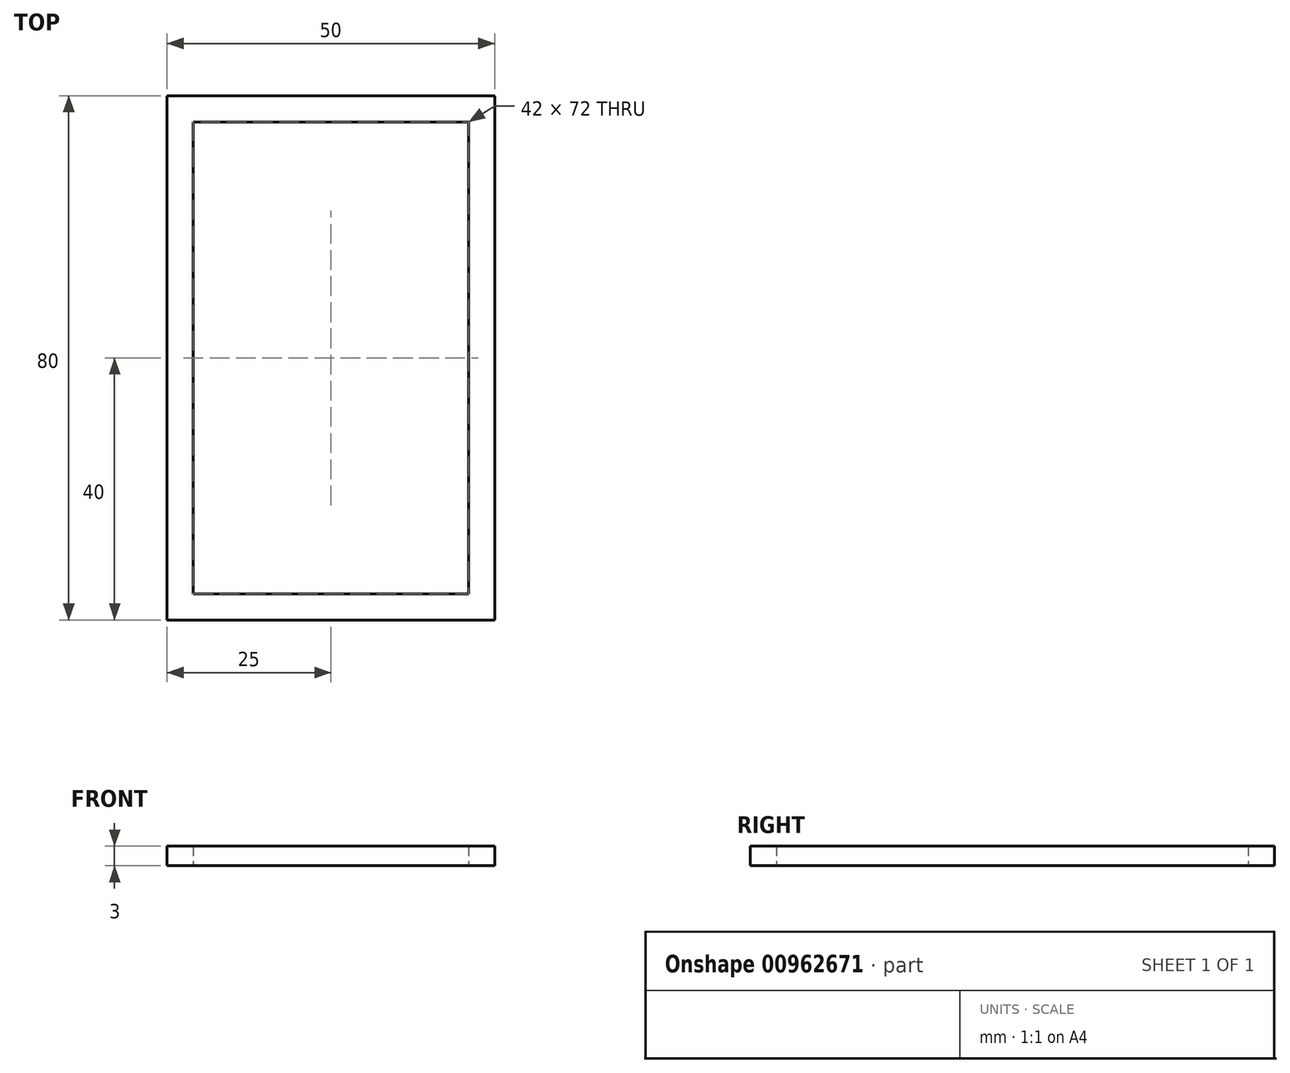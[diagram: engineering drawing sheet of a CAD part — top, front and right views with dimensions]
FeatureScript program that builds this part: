
annotation { "Feature Type Name" : "Feature", "Feature Type Description" : "" }
export const myFeature = defineFeature(function(context is Context, id is Id, definition is map)
    precondition{}
    {
        {
            var Q0;
            Q0=qCreatedBy(makeId("Top.planeOp"),FACE);
            var sketch = newSketch(context, id + "F0", { "sketchPlane" : qUnion([Q0])});
            skLineSegment(sketch, "E0", {"start": v(-25, 40) * mm, "end": v(-25, -40) * mm});
            skLineSegment(sketch, "E1", {"start": v(-25, -40) * mm, "end": v(25, -40) * mm});
            skLineSegment(sketch, "E2", {"start": v(25, -40) * mm, "end": v(25, 40) * mm});
            skLineSegment(sketch, "E3", {"start": v(25, 40) * mm, "end": v(-25, 40) * mm});
            skLineSegment(sketch, "E4", {"start": v(-21, 36) * mm, "end": v(-21, -36) * mm});
            skLineSegment(sketch, "E5", {"start": v(-21, -36) * mm, "end": v(21, -36) * mm});
            skLineSegment(sketch, "E6", {"start": v(21, -36) * mm, "end": v(21, 36) * mm});
            skLineSegment(sketch, "E7", {"start": v(21, 36) * mm, "end": v(-21, 36) * mm});
            skLineSegment(sketch, "E8", {"start": v(-21, 0) * mm, "end": v(-25, 0) * mm, "construction": true});
            skLineSegment(sketch, "E9", {"start": v(0, -36) * mm, "end": v(0, -40) * mm, "construction": true});
            skPoint(sketch, "E9.endSnap0", {"position": v(0, -40) * mm});
            skLineSegment(sketch, "E10", {"start": v(21, 0) * mm, "end": v(25, 0) * mm, "construction": true});
            skLineSegment(sketch, "E11", {"start": v(0, 36) * mm, "end": v(0, 40) * mm, "construction": true});
            skSolve(sketch);
        }
        {
            var Q0;
            Q0=makeQuery(id+"F0.imprint","IMPRINT",FACE,{"disambiguationData":[TD([[makeQuery(id+"F0.imprint","IMPRINT",EDGE,{"derivedFrom":sQuery(id+"F0.wireOp",EDGE,"E0")}),1.0]])]});
            extrude(context, id + "F1", {"entities" : qUnion([Q0]), "depth" : 3 * mm, "offsetDistance" : 25.4 * mm});
        }
    });
